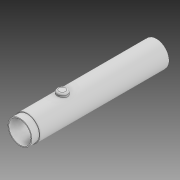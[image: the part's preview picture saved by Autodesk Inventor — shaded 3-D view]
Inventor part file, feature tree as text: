
AUTODESK INVENTOR PART (.ipt)
format: ipt  version: 2020 (Build 240168000, 168)  size: 122,368 bytes
history: native  units: mm
features: sketch x2, revolve x1, extrude x1, fillet x1
ambient origin geometry x8: Origin, YZ Plane, XZ Plane, XY Plane, X Axis, Y Axis, Z Axis, Center Point
bodies: Solid1 (feature_tree)
feature tree (5):
  revolve  "Revolution1"  [1 undecoded]
  extrude  "Extrusion1"  Depth=1.0mm
  fillet  "Fillet1"  Radius=2.25mm
  sketch  "Sketch1"  dims[d0=6.95mm d1=6.6mm]
  sketch  "Sketch2"  dims[d2=4.0mm d4=76.9mm d5=2.25mm d6=1.5mm d7=2.0mm d8=90.0deg d9=0.5mm d10=15.0mm d11=26.0mm d12=5.5mm d13=8.5mm d14=0.0mm d15=1.0mm]
note: 1 required parameter value undecoded (feature->parameter linkage not recoverable at this tier; creation-order binding heuristic only, values carry confidence <= 0.55)
